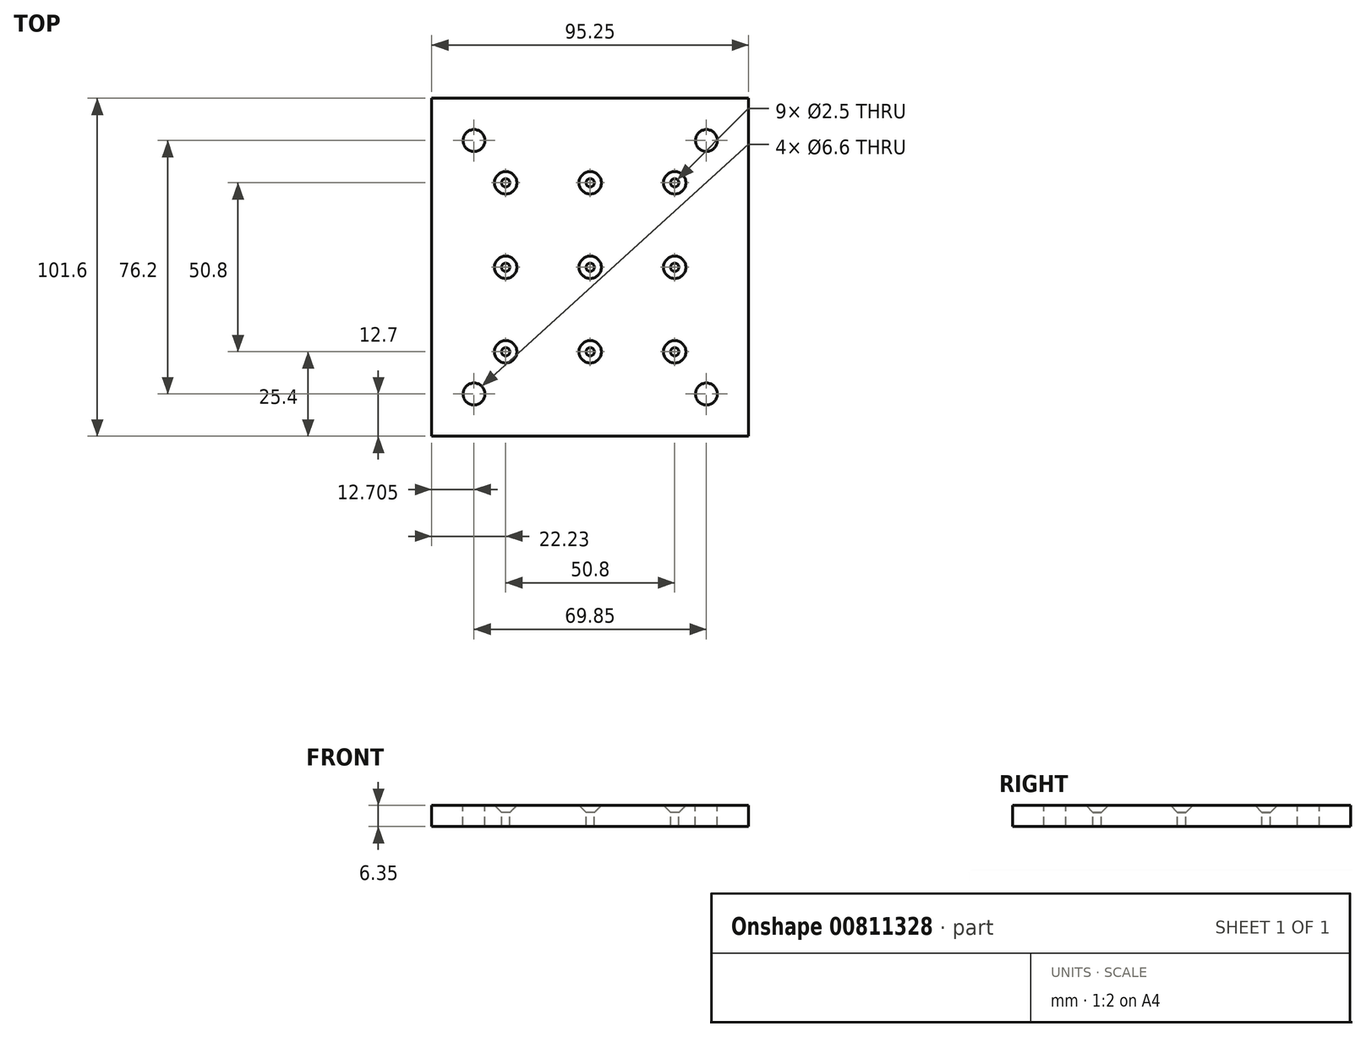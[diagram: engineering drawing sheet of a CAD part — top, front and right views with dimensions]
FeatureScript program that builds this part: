
annotation { "Feature Type Name" : "Feature", "Feature Type Description" : "" }
export const myFeature = defineFeature(function(context is Context, id is Id, definition is map)
    precondition{}
    {
        {
            var Q0;
            Q0=qCreatedBy(makeId("Top.planeOp"),FACE);
            var sketch = newSketch(context, id + "F0", { "sketchPlane" : qUnion([Q0])});
            skLineSegment(sketch, "E0.bottom", {"start": v(-128.07, 50.8) * mm, "end": v(-32.82, 50.8) * mm});
            skLineSegment(sketch, "E0.top", {"start": v(-128.07, -50.8) * mm, "end": v(62.43, -50.8) * mm});
            skLineSegment(sketch, "E0.left", {"start": v(-128.07, 50.8) * mm, "end": v(-128.07, -50.8) * mm});
            skLineSegment(sketch, "E0.right", {"start": v(62.43, 50.8) * mm, "end": v(62.43, -50.8) * mm});
            skPoint(sketch, "E0.middle", {"position": v(-32.82, 0) * mm});
            skLineSegment(sketch, "E1", {"start": v(-115.37, 50.8) * mm, "end": v(-115.37, 38.1) * mm, "construction": true});
            skLineSegment(sketch, "E2", {"start": v(-115.37, 38.1) * mm, "end": v(-128.07, 38.1) * mm, "construction": true});
            skLineSegment(sketch, "E3.MirrorCS", {"start": v(-115.37, -38.1) * mm, "end": v(-128.07, -38.1) * mm, "construction": true});
            skLineSegment(sketch, "E4.MirrorCS", {"start": v(-115.37, -50.8) * mm, "end": v(-115.37, -38.1) * mm, "construction": true});
            skLineSegment(sketch, "E5", {"start": v(-32.82, 0) * mm, "end": v(-32.82, 106.9) * mm, "construction": true});
            skPoint(sketch, "E6.MirrorP", {"position": v(30.69, 0) * mm});
            skPoint(sketch, "E7.MirrorP", {"position": v(56.09, -25.4) * mm});
            skPoint(sketch, "E8.MirrorP", {"position": v(30.69, -25.4) * mm});
            skPoint(sketch, "E9.MirrorP", {"position": v(30.69, 25.4) * mm});
            skPoint(sketch, "E10.MirrorP", {"position": v(5.28, 0) * mm});
            skPoint(sketch, "E11.MirrorP", {"position": v(5.28, 25.4) * mm});
            skLineSegment(sketch, "E12.MirrorCS", {"start": v(49.73, -38.1) * mm, "end": v(62.43, -38.1) * mm, "construction": true});
            skPoint(sketch, "E13.MirrorP", {"position": v(56.09, 0) * mm});
            skLineSegment(sketch, "E14.MirrorCS", {"start": v(49.73, 38.1) * mm, "end": v(62.43, 38.1) * mm, "construction": true});
            skPoint(sketch, "E15.MirrorP", {"position": v(5.28, -25.4) * mm});
            skLineSegment(sketch, "E16.MirrorCS", {"start": v(49.73, -50.8) * mm, "end": v(49.73, -38.1) * mm, "construction": true});
            skLineSegment(sketch, "E17.MirrorCS", {"start": v(49.73, 50.8) * mm, "end": v(49.73, 38.1) * mm, "construction": true});
            skPoint(sketch, "E18.MirrorP", {"position": v(56.09, 25.4) * mm});
            skLineSegment(sketch, "E19", {"start": v(-32.82, 50.8) * mm, "end": v(-32.82, -50.8) * mm});
            skLineSegment(sketch, "E20", {"start": v(-96.32, -50.8) * mm, "end": v(-96.32, -68.95) * mm});
            skLineSegment(sketch, "E21.trimOffspring", {"start": v(49.73, 50.8) * mm, "end": v(62.43, 50.8) * mm});
            skLineSegment(sketch, "E22", {"start": v(-80.44, 50.8) * mm, "end": v(-80.44, -50.8) * mm, "construction": true});
            skLineSegment(sketch, "E23.MirrorCS", {"start": v(-45.52, 50.8) * mm, "end": v(-45.52, 38.1) * mm, "construction": true});
            skLineSegment(sketch, "E24.MirrorCS", {"start": v(-45.52, 38.1) * mm, "end": v(-32.82, 38.1) * mm, "construction": true});
            skLineSegment(sketch, "E25.MirrorCS", {"start": v(-45.52, -38.1) * mm, "end": v(-32.82, -38.1) * mm, "construction": true});
            skLineSegment(sketch, "E26.MirrorCS", {"start": v(-45.52, -50.8) * mm, "end": v(-45.52, -38.1) * mm, "construction": true});
            skPoint(sketch, "E27", {"position": v(-80.44, 0) * mm});
            skPoint(sketch, "E28", {"position": v(-55.04, 0) * mm});
            skPoint(sketch, "E29", {"position": v(-55.04, 25.4) * mm});
            skPoint(sketch, "E30", {"position": v(-80.44, 25.4) * mm});
            skPoint(sketch, "E31.MirrorP", {"position": v(-105.84, 25.4) * mm});
            skPoint(sketch, "E32.MirrorP", {"position": v(-105.84, 0) * mm});
            skPoint(sketch, "E33.MirrorP", {"position": v(-55.04, -25.4) * mm});
            skPoint(sketch, "E34.MirrorP", {"position": v(-80.44, -25.4) * mm});
            skPoint(sketch, "E35.MirrorP", {"position": v(-105.84, -25.4) * mm});
            skSolve(sketch);
        }
        {
            var Q0;
            Q0=makeQuery(id+"F0.imprint","IMPRINT",FACE,{"disambiguationData":[TD([[makeQuery(id+"F0.imprint","IMPRINT",EDGE,{"derivedFrom":sQuery(id+"F0.wireOp",EDGE,"E0.bottom")}),-1.0]])]});
            extrude(context, id + "F1", {"entities" : qUnion([Q0]), "oppositeDirection" : true, "depth" : 6.35 * mm, "offsetDistance" : 25.4 * mm});
        }
        {
            var Q0;
            Q0=sQuery(id+"F0.wireOp",VERTEX,"E1.end");
            var Q1;
            Q1=sQuery(id+"F0.wireOp",VERTEX,"E23.MirrorCS.end");
            var Q2;
            Q2=sQuery(id+"F0.wireOp",VERTEX,"E25.MirrorCS.start");
            var Q3;
            Q3=sQuery(id+"F0.wireOp",VERTEX,"E3.MirrorCS.start");
            var Q4;
            Q4=makeQuery(id+"F1.opExtrude","SWEPT_BODY",BODY,{"disambiguationData":[OSD([sQuery(id+"F0.wireOp",EDGE,"E0.bottom"),sQuery(id+"F0.wireOp",EDGE,"E0.top"),sQuery(id+"F0.wireOp",EDGE,"E0.left"),sQuery(id+"F0.wireOp",EDGE,"E19")])]});
            hole(context, id + "F2", {"style" : HoleStyle.SIMPLE, "endStyle" : HoleEndStyle.BLIND, "standardTappedOrClearance" : lookupTablePath({ "standard" : "ISO", "fit" : "Normal", "size" : "M6", "type" : "Clearance" }), "standardBlindInLast" : lookupTablePath({ "fit" : "Standard", "standard" : "ISO", "size" : "M6", "type" : "Clearance" }), "holeDiameter" : 6.6 * mm, "majorDiameter" : 6.35 * mm, "holeDepth" : 12.7 * mm, "isTappedThrough" : true, "tappedDepth" : 11.2 * mm, "tapClearance" : 3, "locations" : qUnion([Q0, Q1, Q2, Q3]), "scope" : qUnion([Q4])});
        }
        {
            var Q0;
            Q0=sQuery(id+"F0.wireOp",VERTEX,"E31.MirrorP");
            var Q1;
            Q1=sQuery(id+"F0.wireOp",VERTEX,"E30");
            var Q2;
            Q2=sQuery(id+"F0.wireOp",VERTEX,"E29");
            var Q3;
            Q3=sQuery(id+"F0.wireOp",VERTEX,"E27");
            var Q4;
            Q4=sQuery(id+"F0.wireOp",VERTEX,"E28");
            var Q5;
            Q5=sQuery(id+"F0.wireOp",VERTEX,"E32.MirrorP");
            var Q6;
            Q6=sQuery(id+"F0.wireOp",VERTEX,"E35.MirrorP");
            var Q7;
            Q7=sQuery(id+"F0.wireOp",VERTEX,"E34.MirrorP");
            var Q8;
            Q8=sQuery(id+"F0.wireOp",VERTEX,"E33.MirrorP");
            var Q9;
            Q9=makeQuery(id+"F1.opExtrude","SWEPT_BODY",BODY,{"disambiguationData":[OSD([sQuery(id+"F0.wireOp",EDGE,"E0.bottom"),sQuery(id+"F0.wireOp",EDGE,"E0.top"),sQuery(id+"F0.wireOp",EDGE,"E0.left"),sQuery(id+"F0.wireOp",EDGE,"E19")])]});
            hole(context, id + "F3", {"style" : HoleStyle.C_SINK, "endStyle" : HoleEndStyle.BLIND, "standardTappedOrClearance" : lookupTablePath({ "standard" : "ISO", "engagement" : "75%", "pitch" : "0.5 mm", "size" : "M3", "type" : "Tapped" }), "standardBlindInLast" : lookupTablePath({ "standard" : "ISO", "engagement" : "75%", "pitch" : "0.5 mm", "size" : "M3", "type" : "Tapped" }), "holeDiameter" : 2.5 * mm, "cSinkDiameter" : 6.72 * mm, "cSinkAngle" : 90 * degree, "majorDiameter" : 3 * mm, "showTappedDepth" : true, "holeDepth" : 12.7 * mm, "isTappedThrough" : true, "tappedDepth" : 11.2 * mm, "tapClearance" : 3, "locations" : qUnion([Q0, Q1, Q2, Q3, Q4, Q5, Q6, Q7, Q8]), "scope" : qUnion([Q9])});
        }
    });
